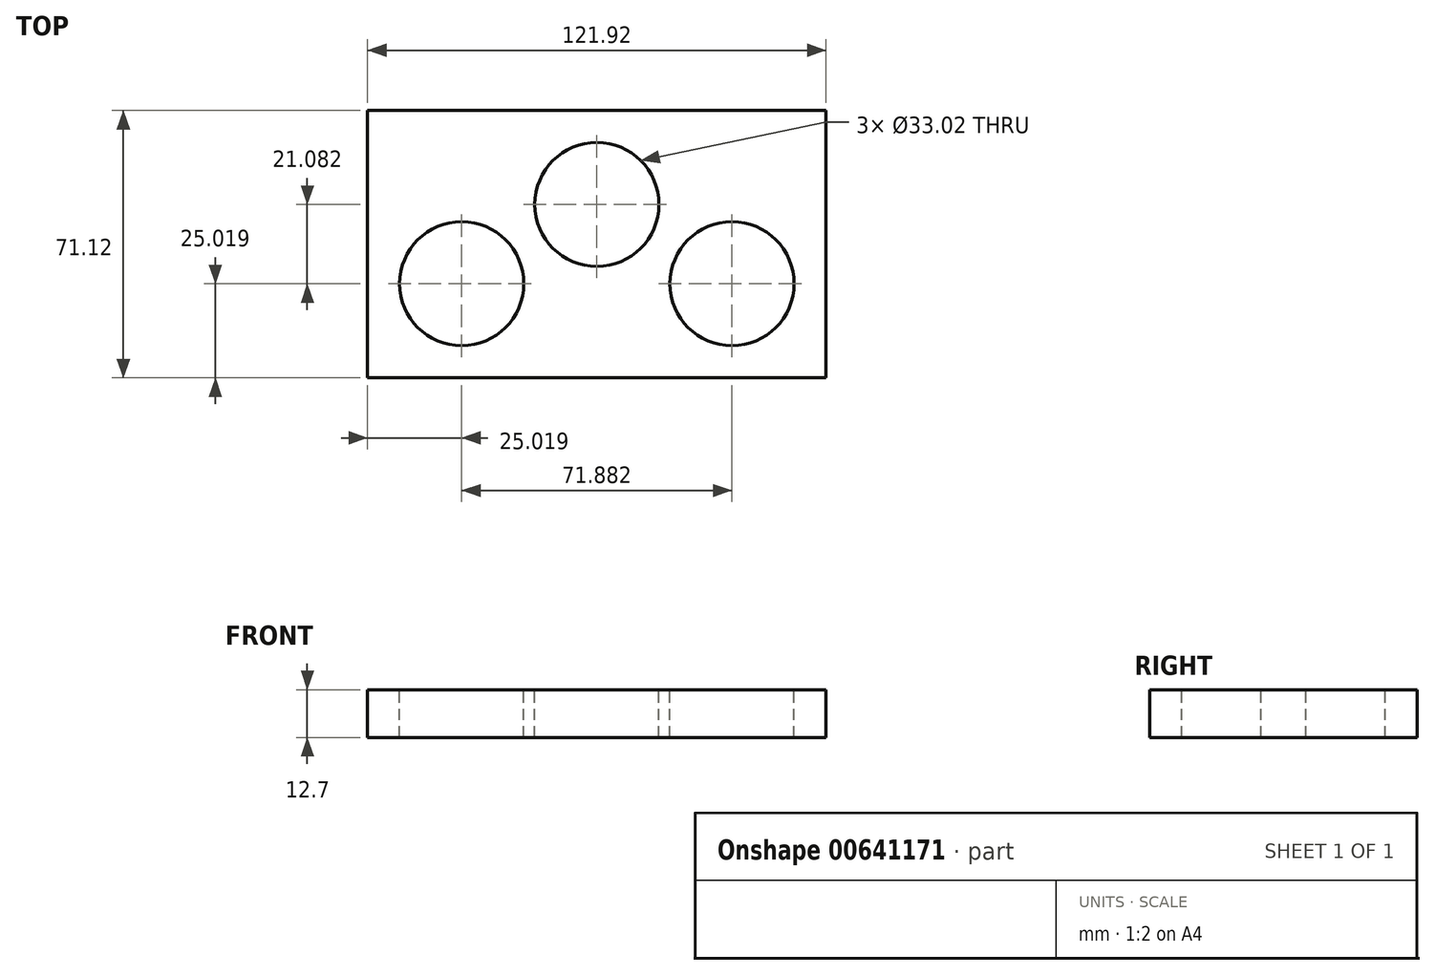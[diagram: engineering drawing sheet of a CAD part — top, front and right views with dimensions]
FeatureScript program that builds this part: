
annotation { "Feature Type Name" : "Feature", "Feature Type Description" : "" }
export const myFeature = defineFeature(function(context is Context, id is Id, definition is map)
    precondition{}
    {
        {
            var Q0;
            Q0=qCreatedBy(makeId("Top.planeOp"),FACE);
            var sketch = newSketch(context, id + "F0", { "sketchPlane" : qUnion([Q0])});
            skLineSegment(sketch, "E0.bottom", {"start": v(-60.96, -35.56) * mm, "end": v(60.96, -35.56) * mm});
            skLineSegment(sketch, "E0.top", {"start": v(-60.96, 35.56) * mm, "end": v(60.96, 35.56) * mm});
            skLineSegment(sketch, "E0.left", {"start": v(-60.96, -35.56) * mm, "end": v(-60.96, 35.56) * mm});
            skLineSegment(sketch, "E0.right", {"start": v(60.96, -35.56) * mm, "end": v(60.96, 35.56) * mm});
            skPoint(sketch, "E0.middle", {"position": v(0, 10.54) * mm});
            skCircle(sketch, "E1", {"center": v(-35.94, -10.54) * mm, "radius": 16.51 * mm});
            skCircle(sketch, "E2", {"center": v(0, 10.54) * mm, "radius": 16.51 * mm});
            skCircle(sketch, "E3", {"center": v(35.94, -10.54) * mm, "radius": 16.51 * mm});
            skSolve(sketch);
        }
        {
            var Q0;
            Q0=makeQuery(id+"F0.imprint","IMPRINT",FACE,{"disambiguationData":[TD([[makeQuery(id+"F0.imprint","IMPRINT",EDGE,{"derivedFrom":sQuery(id+"F0.wireOp",EDGE,"E0.bottom")}),1.0]])]});
            extrude(context, id + "F1", {"entities" : qUnion([Q0]), "oppositeDirection" : true, "depth" : 12.7 * mm, "offsetDistance" : 25.4 * mm});
        }
    });
